# Revit family: Lighting-ArredoUrbano-GEWISS-URBAN[O3]-LED-SBRACCIGW_OTTICA_CICLOPEDONALE
name_source: partatom
category: Apparecchi per illuminazione
units: mm (PartAtom-declared; Revit-internal decimal feet)

## family parameters
Condiviso = No
Host = Superficie
Numero OmniClass = 23.80.70.00
Punto di calcolo locali = Sì
Quota connettore circolare = Usa diametro
Sorgente d'illuminazione = No
Taglio con vuoti quando caricato = No
Tipo di parte = Normale
Titolo OmniClass = Lighting

## types (1)
- Lighting-ArredoUrbano-GEWISS-URBAN[O3]-LED-SBRACCIGW_OTTICA_CICLOPEDONALE
    Adatto per = Sbracci Gewiss
    Adatto per: = Sbracci Gewiss
    Applicazione = Esterno
    Catalogo = LIGHTING
    Catalogo Serie = URBAN [O3]
    Classe isolamento = II
    Codice EAN = 8011564868946
    Codice Electrocod = 244C
    Colore = Blu notte
    Corrente di pilotaggio = 530mA
    Corrente di pilotaggio LED = 530mA
    Descrizione = URBAN LED 3M 3500K SBRACCI GW CICLOPEDONALE BLU
    Distanza minima dall'oggetto illuminato = 1M
    Finitura = GEWISS - BLU NOTTE
    Flusso nominale (lm) = 5760
    Garanzia = 5 anni
    Grado di protezione = IP66
    IDF = d8fedbbd-84cd-4dc8-bdd0-0df7432b89f4
    IDT = a19afcb9-5bbe-476a-b188-1c900bde322b
    Immagine tipo = GW87908.jpg
    LED Life time (L80B10) = 100000H
    LED LifeTime (L80B20) = 50000h
    LED LifeTime (L90B20) = 50000H
    Lumen output (lm) = 4740
    Modello = GWS7502B
    N. moduli Chorus = 3 (3x16 LED)
    Numero moduli = 3 (3x16 LED)
    Ottica = Ciclopedonale - ULOR: 0%
    Peso (kg) = 8,8
    Peso (kg): = 8,8
    Potenza di sistema = 81W
    Produttore = GEWISS S.p.A.
    Prospetto di default = 1219 mm
    Resistenza agli urti = IK08 CORPO - IK06 LENTI
    Rischio fotobiologico = RG1/RG2 @ 20cm
    Rischio fotobiologico: = RG1/RG2 @ 20cm
    SEO = Stradale
    Scheda Tecnica = https://www.gewiss.com
    Superficie massima esposta al vento = 0,25M2
    Temperatura di colore = 3500 K (CRI 85)
    Temperatura di colore: = 3500 K (CRI 85)
    Temperatura di funzionamento = -25 +35 °C
    Temperatura di utilizzo = -25 +35 °C
    Tensione = 220/240 V - 50/60 Hz - Stand alone e/o dimmerabile 1-10 V
    Tensione: = 220/240 V - 50/60 Hz
    Tipo alimentatore = Driver Led in corrente continua
    Tipologia lampada = LED
    Tipologia sorgente luminosa = LED
    URL = https://www.gewiss.com
    Versione file RFA = 20.11
    Vetro = GEWISS - VETRO

## geometry (parser evidence)
native form markers: Blend x4
no freeform markers — native parametric forms only
